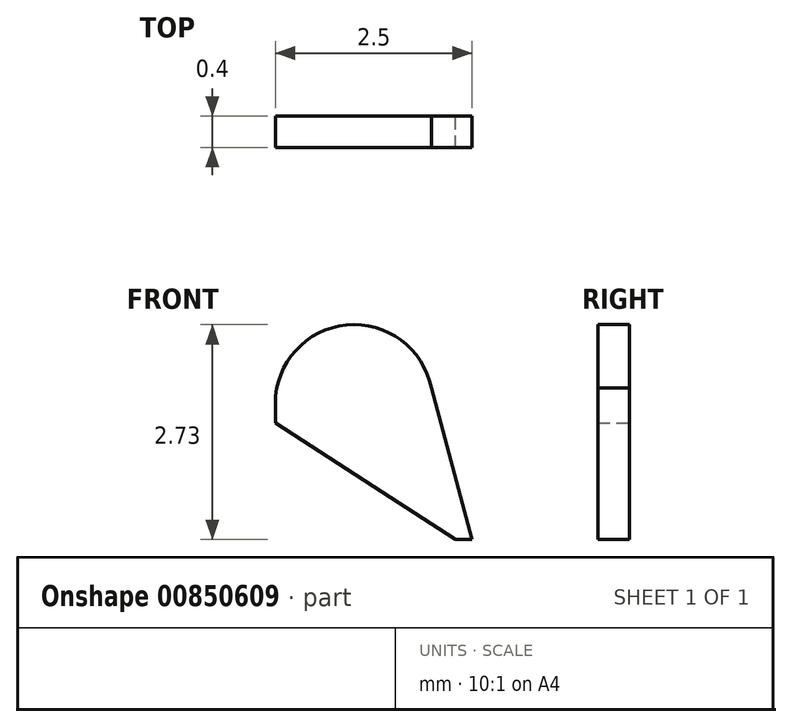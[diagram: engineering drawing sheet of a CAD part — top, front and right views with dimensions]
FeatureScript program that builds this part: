
annotation { "Feature Type Name" : "Feature", "Feature Type Description" : "" }
export const myFeature = defineFeature(function(context is Context, id is Id, definition is map)
    precondition{}
    {
        {
            var Q0;
            Q0=qCreatedBy(makeId("Front.planeOp"),FACE);
            var sketch = newSketch(context, id + "F0", { "sketchPlane" : qUnion([Q0])});
            skArc(sketch, "E0", {"start": v(-1, 0) * mm, "mid": v(-0.1, 1) * mm, "end": v(0.98, 0.2) * mm});
            skLineSegment(sketch, "E1", {"start": v(-1, 0) * mm, "end": v(-1, -0.25) * mm});
            skLineSegment(sketch, "E2", {"start": v(1.3, -1.73) * mm, "end": v(0.35, -1.12) * mm, "construction": true});
            skLineSegment(sketch, "E3", {"start": v(1.5, -1.73) * mm, "end": v(0.94, 0.33) * mm});
            skLineSegment(sketch, "E4", {"start": v(1.3, -1.73) * mm, "end": v(0.35, -1.12) * mm});
            skLineSegment(sketch, "E5", {"start": v(-1, -0.25) * mm, "end": v(0.35, -1.12) * mm});
            skPoint(sketch, "E6.start.orphan", {"position": v(1, 0) * mm});
            skPoint(sketch, "E7.end.orphan", {"position": v(-1, -1.32) * mm});
            skPoint(sketch, "E7.start.orphan", {"position": v(-0.2, -0.77) * mm});
            skLineSegment(sketch, "E8", {"start": v(1.3, -1.73) * mm, "end": v(1.5, -1.73) * mm});
            skLineSegment(sketch, "E9", {"start": v(0, 1) * mm, "end": v(0, 0) * mm, "construction": true});
            skSolve(sketch);
        }
        {
            var Q0;
            Q0 = qSketchRegion(id + "F0", true);
            extrude(context, id + "F1", {"entities" : qUnion([Q0]), "depth" : 0.4 * mm, "offsetDistance" : 25 * mm});
        }
    });
